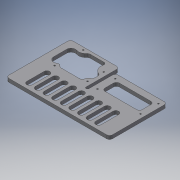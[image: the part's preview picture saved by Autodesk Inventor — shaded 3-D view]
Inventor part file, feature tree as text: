
AUTODESK INVENTOR PART (.ipt)
format: ipt  version: 2017 (Build 210142000, 142)  size: 287,232 bytes
history: native  units: mm
features: sketch x6, extrude x5, plane x4, reference x4, hole x3, fillet x3, other x3, pattern_linear x1, mirror x1
ambient origin geometry x8: Origin, YZ Plane, XZ Plane, XY Plane, X Axis, Y Axis, Z Axis, Center Point
bodies: Solid1 (feature_tree)
feature tree (30):
  extrude  "Extrusion1"  Depth=180.0mm
  plane  "Work Plane1"
  hole  "Hole2"  [1 undecoded]
  extrude  "Extrusion2"  TaperAngle=0.0deg  [1 undecoded]
  plane  "Work Plane4"
  hole  "Hole3"  [1 undecoded]
  extrude  "Extrusion3"  Depth=48.0mm
  fillet  "Fillet1"  Radius=6.0mm
  pattern_linear  "Rectangular Pattern1"  Spacing1=31.0mm  [1 undecoded]
  mirror  "Mirror1"
  plane  "Work Plane2"
  extrude  "Extrusion4"  Depth=10.0mm
  plane  "Work Plane3"
  extrude  "Extrusion5"  Depth=40.0mm
  fillet  "Fillet2"  Radius=10.0mm
  hole  "Hole4"  [1 undecoded]
  fillet  "Fillet3"  Radius=5.0mm
  sketch  "Sketch1"  dims[d0=6.0mm d1=0.0mm d2=180.0mm]
  sketch  "Sketch5"  dims[d3=52.0mm d6=85.0mm]
  sketch  "Sketch8"  dims[d7=60.0mm d8=0.0mm]
  sketch  "Sketch9"  dims[d18=2.5mm d19=6.0mm d20=4.0mm d21=2.0mm d22=90.0deg d23=8.0mm d24=20.594885mm d25=90.0mm]
  sketch  "Sketch10"  dims[d26=0.0mm d27=48.0mm d28=6.0mm d29=0.0mm]
  reference  "Reference9"
  reference  "Reference10"
  reference  "Reference11"
  reference  "Reference12"
  sketch  "Sketch13"  dims[d32=75.0mm d33=31.0mm d36=2.5mm d37=6.0mm d38=4.0mm d39=2.0mm d40=90.0deg d41=8.0mm d42=20.594885mm d43=10.0mm d44=40.0mm d45=10.0mm d46=0.0mm d47=50.0mm d49=15.0mm d50=5.0mm d51=5.0mm d52=6.0mm d53=0.0mm d54=5.0mm d55=6.0mm d56=0.0mm d67=5.0mm d68=8.0mm d69=8.0mm d70=90.0deg d71=25.0mm d72=65.0mm d73=75.0mm d74=5.0mm d76=31.0mm d77=3.0mm d78=6.0mm d79=6.0mm d80=4.0mm d81=2.0mm d82=90.0deg d83=3.0mm d84=0.0mm d85=5.0mm d86=2.0mm]
  other  "<userpath>\Google Drive\Metal Class Projetos\Base Arduino\Montagem_Arduino.iam"
  other  "Montagem_Arduino.iam"
  other  "ArduinoUNO :2"
note: 5 required parameter values undecoded (feature->parameter linkage not recoverable at this tier; creation-order binding heuristic only, values carry confidence <= 0.55)
